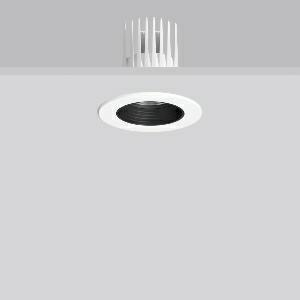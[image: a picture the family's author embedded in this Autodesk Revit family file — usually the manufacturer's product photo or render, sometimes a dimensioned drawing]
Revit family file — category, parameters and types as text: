
# Revit family: heledon_mini_e_901752_002_76_5620
name_source: partatom
category: Lighting Fixtures
units: mm (PartAtom-declared; Revit-internal decimal feet)

## family parameters
Cut with Voids When Loaded = No
Host = Face
Light Source = No
Part Type = Normal
Room Calculation Point = No
Round Connector Dimension = Use Diameter
Shared = No

## types (1)
- HELEDON mini E (1 x LED Modul 930, 3000 lm, 3000)
    Apparent Load = 29 VA
    Approval mark = CE
    CIE Flux Codes = 96 100 100 100 100
    Color Rendering = 90
    Color Temperature = 3000
    Default Elevation = 1800 mm
    Description = Series: HELEDON mini
Round recessed downlight. Housing: die-cast aluminium, powder-coated. Black plastic ring and recessed LED to prevent glare from the side. Optical assembly with lens made of plastic (polycarbonate) for the best homogeneous light distribution - can be changed without tools. Best colour rendering index Ra>90. Suitable for Recessed ceiling mounting. Installation without tools thanks to spring fastening system. Including separate LED converter with connecting cable 600 mm.High quality converter without flickering and stroboscopic effect. Through-wiring box (5 pole) available as accessory. The following accessories can be mounted without use of tools: interchangeable lenses, decorative glasses, honeycomb louvre, clear and frosted diffusers, white interchangeable plastic ring. 
Colour: traffic white, matt (RAL 9016)
Diameter: 124 mm
Height: 3 mm
Cut-out diameter: 114 mm
Recess height: 170 mm
Luminaire: recess height: 120 mm
Lamp: LED
Socket: without socket
Colour temperature: 3000K
Colour rendering index (CRI): 92
System power: 29 W
Rated luminous flux: 3000 lm
Luminous efficiency: 103 lm/W
Control gear: Converter, dimmable, DALI
Protection class: II
Type of protection: IP 20
    Height = 0 mm  [stored 0 ft]
    Lamp = 1 x LED Modul 930
    Lamp Light Flux = 3000 lm
    Lamp count = 1
    Length = 124 mm  [stored 0.406824 ft]
    Lifetime = 50000 h
    Luminous efficacy = 103 lm/W
    Manufacturer = RZB
    ModVariant = No
    Model = 901752.002.76
    Mounting Place = Ceiling
    Mounting Type = Recessed
    Number of Poles = 1
    OnlyDefault = Yes
    Power Factor = 1
    Product Name = HELEDON mini E
    Product group = Recessed downlights
    ProductGroupID = 402
    Protection Class = Protection class II
    Protection Degree = IP 20
    RLX_Detail_Level = 1
    RLX_Emergency_Light_Flux = 0 lm
    RLX_Emergency_Type = 0
    RLX_Emergency_Type_DB = No
    RlxData = <blob elided: 123637 chars, md5=2cdee5f1>
    Socket = socket
    Standby Power = 0 W
    System Light Flux = 3000 lm
    System Power = 29 W
    Type Comments = Product without accessories
    Type Image = 901656.002.jpg
    URL = http://relux.com
    VarID = ---
    Voltage = 230 V
    Voltage Range = 220-240 V
    Weight = 0.00 kg
    Width = 0 mm  [stored 0 ft]

note: [stored X ft] marks values corroborated as IEEE doubles in the binary element streams (Revit-internal decimal feet)

## geometry (parser evidence)
native form markers: Blend x4, Sweep x9
no freeform markers — native parametric forms only
